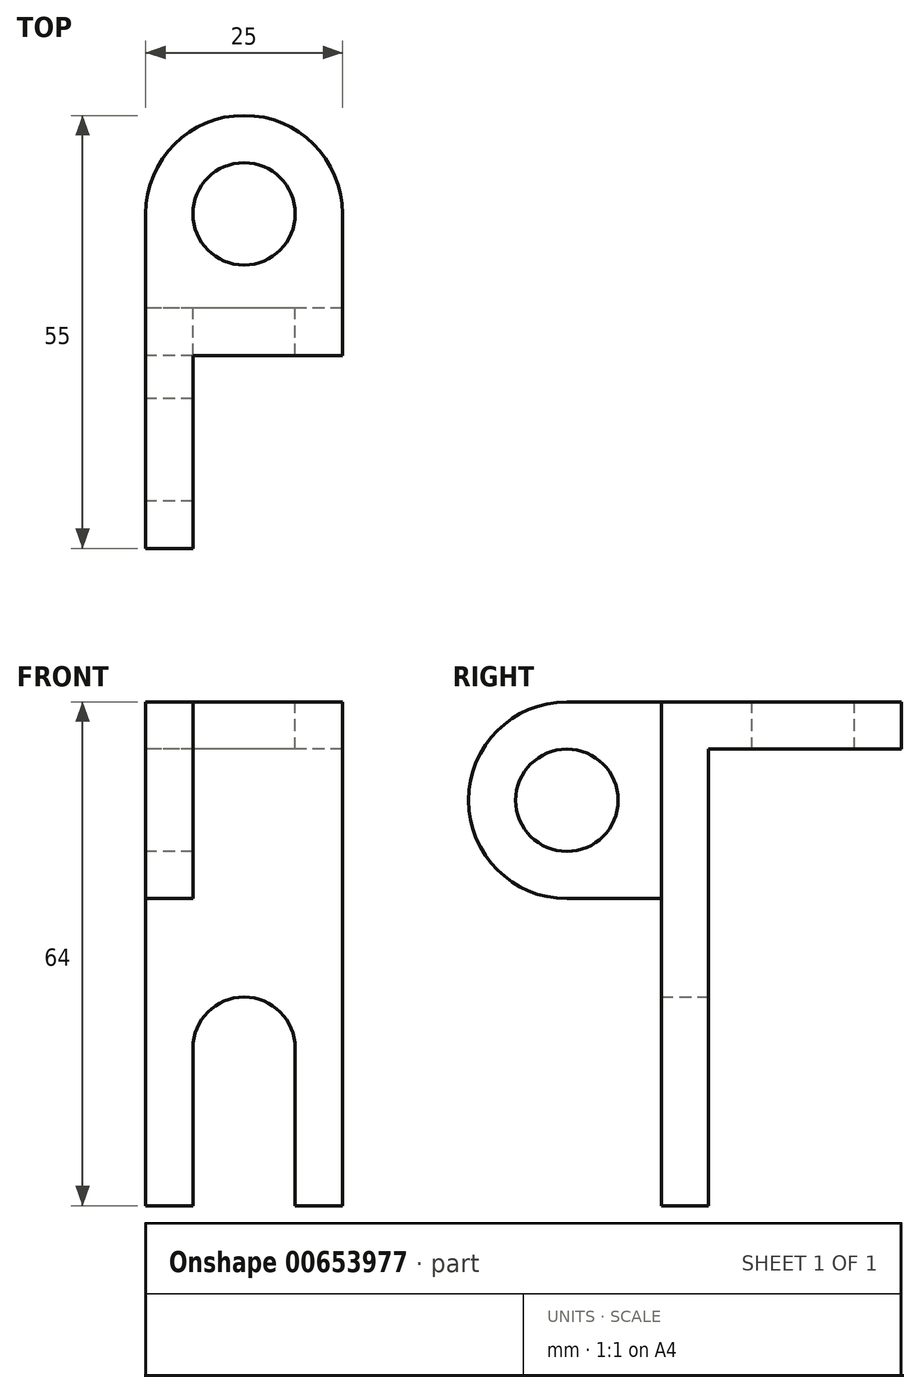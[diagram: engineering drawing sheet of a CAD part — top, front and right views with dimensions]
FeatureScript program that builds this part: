
annotation { "Feature Type Name" : "Feature", "Feature Type Description" : "" }
export const myFeature = defineFeature(function(context is Context, id is Id, definition is map)
    precondition{}
    {
        {
            var Q0;
            Q0=qCreatedBy(makeId("Front.planeOp"),FACE);
            var sketch = newSketch(context, id + "F0", { "sketchPlane" : qUnion([Q0])});
            skLineSegment(sketch, "E0.bottom", {"start": v(12.5, 32) * mm, "end": v(-12.5, 32) * mm});
            skLineSegment(sketch, "E0.top", {"start": v(12.5, -32) * mm, "end": v(-12.5, -32) * mm});
            skLineSegment(sketch, "E0.left", {"start": v(12.5, 32) * mm, "end": v(12.5, -32) * mm});
            skLineSegment(sketch, "E0.right", {"start": v(-12.5, 32) * mm, "end": v(-12.5, -32) * mm});
            skPoint(sketch, "E0.middle", {"position": v(0, 0) * mm});
            skLineSegment(sketch, "E1.bottom", {"start": v(6.5, -32) * mm, "end": v(-6.5, -32) * mm});
            skLineSegment(sketch, "E1.top", {"start": v(6.5, -12) * mm, "end": v(-6.5, -12) * mm});
            skLineSegment(sketch, "E1.left", {"start": v(6.5, -32) * mm, "end": v(6.5, -12) * mm});
            skLineSegment(sketch, "E1.right", {"start": v(-6.5, -32) * mm, "end": v(-6.5, -12) * mm});
            skPoint(sketch, "E1.middle", {"position": v(0, -22) * mm});
            skCircle(sketch, "E2", {"center": v(0, -12) * mm, "radius": 6.5 * mm});
            skSolve(sketch);
        }
        {
            var Q0;
            Q0=makeQuery(id+"F0.imprint","IMPRINT",FACE,{"disambiguationData":[TD([[makeQuery(id+"F0.imprint","IMPRINT",EDGE,{"derivedFrom":sQuery(id+"F0.wireOp",EDGE,"E0.bottom")}),1.0]])]});
            extrude(context, id + "F1", {"entities" : qUnion([Q0]), "depth" : 6 * mm, "offsetDistance" : 25 * mm});
        }
        {
            var Q0;
            Q0=makeQuery(id+"F1.opExtrude","SWEPT_FACE",FACE,{"disambiguationData":[OSD([sQuery(id+"F0.wireOp",EDGE,"E0.bottom")])]});
            var sketch = newSketch(context, id + "F2", { "sketchPlane" : qUnion([Q0])});
            skLineSegment(sketch, "E3.bottom", {"start": v(12.5, -6) * mm, "end": v(-12.5, -6) * mm});
            skLineSegment(sketch, "E3.top", {"start": v(12.5, 12) * mm, "end": v(6.5, 12) * mm, "construction": true});
            skLineSegment(sketch, "E3.left", {"start": v(12.5, -6) * mm, "end": v(12.5, 12) * mm});
            skLineSegment(sketch, "E3.right", {"start": v(-12.5, -6) * mm, "end": v(-12.5, 12) * mm});
            skCircle(sketch, "E4", {"center": v(0, 12) * mm, "radius": 12.5 * mm});
            skCircle(sketch, "E5", {"center": v(0, 12) * mm, "radius": 6.5 * mm});
            skLineSegment(sketch, "E6.trimOffspring", {"start": v(-6.5, 12) * mm, "end": v(-12.5, 12) * mm, "construction": true});
            skSolve(sketch);
        }
        {
            var Q0;
            Q0 = qSketchRegion(id + "F2", true);
            extrude(context, id + "F3", {"entities" : qUnion([Q0]), "operationType" : NewBodyOperationType.ADD, "oppositeDirection" : true, "depth" : 6 * mm, "offsetDistance" : 25 * mm});
        }
        {
            var Q0;
            Q0=makeQuery(id+"F3.boolean.opBoolean","MERGE",FACE,{"derivedFrom":[makeQuery(id+"F1.opExtrude","SWEPT_FACE",FACE,{"disambiguationData":[OSD([sQuery(id+"F0.wireOp",EDGE,"E0.right")])]}),makeQuery(id+"F3.opExtrude","SWEPT_FACE",FACE,{"disambiguationData":[OSD([sQuery(id+"F2.wireOp",EDGE,"E3.right")])]})]});
            var sketch = newSketch(context, id + "F4", { "sketchPlane" : qUnion([Q0])});
            skLineSegment(sketch, "E7.bottom", {"start": v(0, 32) * mm, "end": v(18, 32) * mm});
            skLineSegment(sketch, "E7.top", {"start": v(0, 7) * mm, "end": v(18, 7) * mm});
            skLineSegment(sketch, "E7.left", {"start": v(0, 32) * mm, "end": v(0, 7) * mm});
            skLineSegment(sketch, "E7.right", {"start": v(18, 32) * mm, "end": v(18, 7) * mm});
            skArc(sketch, "E8", {"start": v(18, 7) * mm, "mid": v(30.5, 19.5) * mm, "end": v(18, 32) * mm});
            skCircle(sketch, "E9", {"center": v(18, 19.5) * mm, "radius": 6.5 * mm});
            skSolve(sketch);
        }
        {
            var Q0;
            {var subQ0=sQuery(id+"F4.wireOp",EDGE,"E8");Q0=makeQuery(id+"F4.imprint","IMPRINT",FACE,{"disambiguationData":[TD([[makeQuery(id+"F4.imprint","IMPRINT",EDGE,{"derivedFrom":subQ0}),1.0]])]});}
            var Q1;
            {var subQ3=sQuery(id+"F4.wireOp",EDGE,"E7.bottom");var subQ4=sQuery(id+"F0.wireOp",EDGE,"E0.right");var subQ8=makeQuery(id+"F1.opExtrude","CAP_EDGE",EDGE,{"disambiguationData":[OSD([subQ4])],"isStart":false});var subQ10=makeQuery(id+"F4.imprint","INTERSECT",VERTEX,{"derivedFrom":[subQ8,subQ3]});Q1=makeQuery(id+"F4.imprint","IMPRINT",FACE,{"disambiguationData":[TD([[makeQuery(id+"F4.imprint","IMPRINT",EDGE,{"disambiguationData":[TD([[subQ10,-1.0]])],"derivedFrom":subQ8}),-1.0]])]});}
            var Q2;
            {var subQ1=sQuery(id+"F4.wireOp",EDGE,"E7.right");var subQ4=sQuery(id+"F4.wireOp",EDGE,"E9");var subQ5=makeQuery(id+"F4.imprint","INTERSECT",VERTEX,{"disambiguationData":[OD(0.0)],"derivedFrom":[subQ1,subQ4]});Q2=makeQuery(id+"F4.imprint","IMPRINT",FACE,{"disambiguationData":[TD([[makeQuery(id+"F4.imprint","IMPRINT",EDGE,{"disambiguationData":[TD([[subQ5,-1.0]])],"derivedFrom":subQ4}),-1.0]])]});}
            extrude(context, id + "F5", {"entities" : qUnion([Q0, Q1, Q2]), "operationType" : NewBodyOperationType.ADD, "oppositeDirection" : true, "depth" : 6 * mm, "offsetDistance" : 25 * mm});
        }
    });
